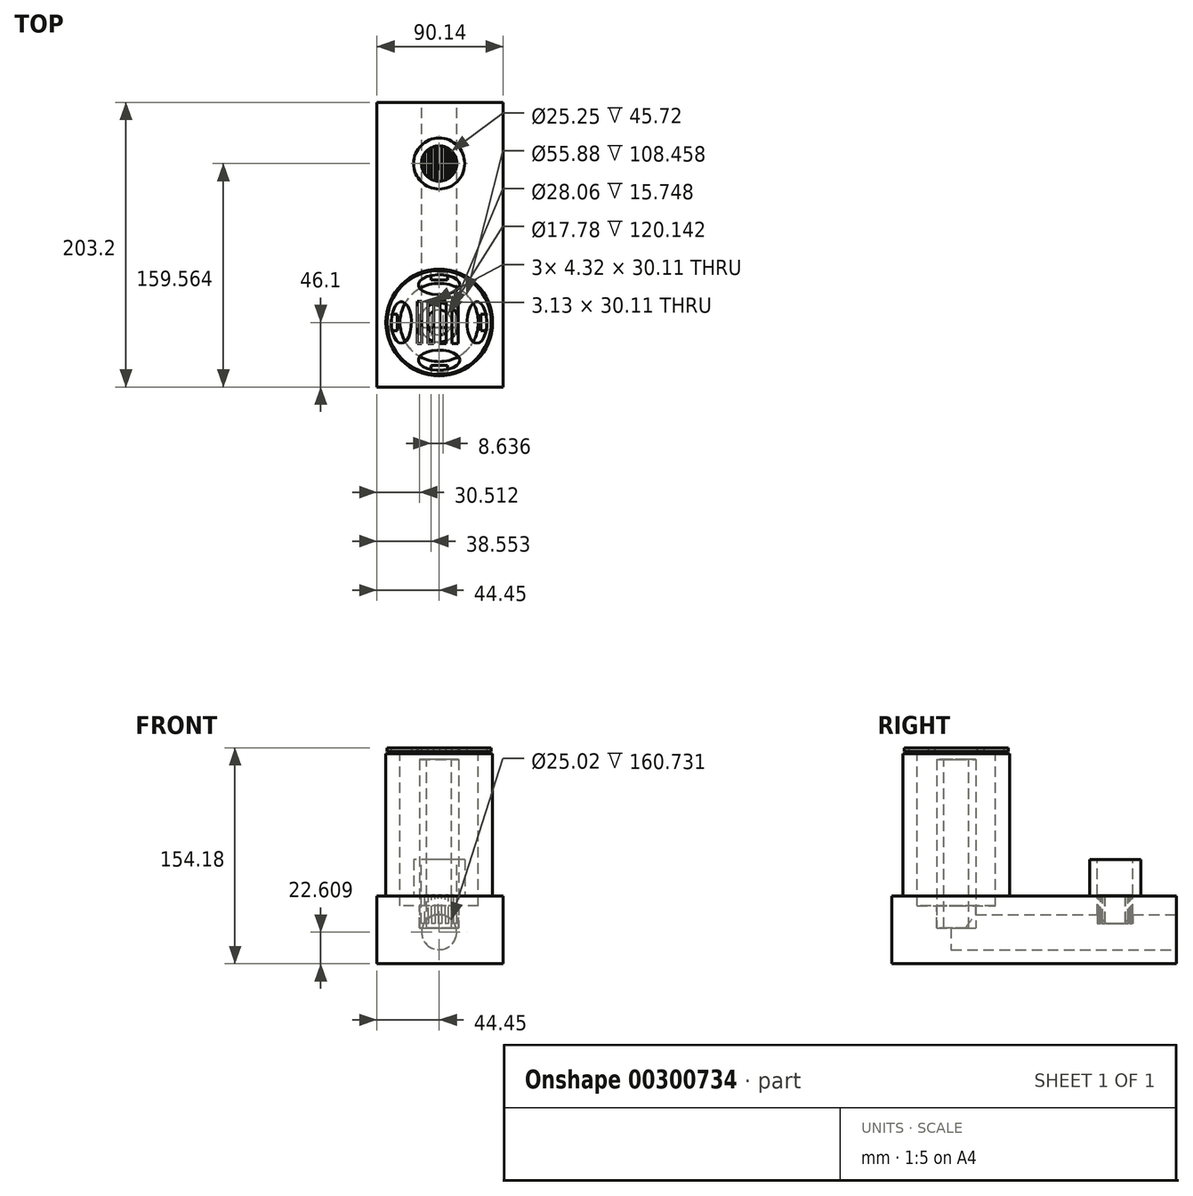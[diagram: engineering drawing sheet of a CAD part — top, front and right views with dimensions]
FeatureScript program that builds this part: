
annotation { "Feature Type Name" : "Feature", "Feature Type Description" : "" }
export const myFeature = defineFeature(function(context is Context, id is Id, definition is map)
    precondition{}
    {
        {
            var Q0;
            Q0=qCreatedBy(makeId("Top.planeOp"),FACE);
            var sketch = newSketch(context, id + "F0", { "sketchPlane" : qUnion([Q0])});
            skCircle(sketch, "E0", {"center": v(0, 0) * mm, "radius": 38.1 * mm});
            skSolve(sketch);
        }
        {
            var Q0;
            Q0=makeQuery(id+"F0.imprint","IMPRINT",FACE,{"disambiguationData":[TD([[makeQuery(id+"F0.imprint","IMPRINT",EDGE,{"derivedFrom":sQuery(id+"F0.wireOp",EDGE,"E0")}),1.0]])]});
            extrude(context, id + "F1", {"entities" : qUnion([Q0]), "depth" : 101.6 * mm});
        }
        {
            var Q0;
            Q0=qCreatedBy(makeId("Top.planeOp"),FACE);
            var sketch = newSketch(context, id + "F2", { "sketchPlane" : qUnion([Q0])});
            skLineSegment(sketch, "E1.bottom", {"start": v(-44.45, -46.1) * mm, "end": v(45.7, -46.1) * mm});
            skLineSegment(sketch, "E1.top", {"start": v(-44.45, 157.1) * mm, "end": v(45.7, 157.1) * mm});
            skLineSegment(sketch, "E1.left", {"start": v(-44.45, -46.1) * mm, "end": v(-44.45, 157.1) * mm});
            skLineSegment(sketch, "E1.right", {"start": v(45.7, -46.1) * mm, "end": v(45.7, 157.1) * mm});
            skSolve(sketch);
        }
        {
            var Q0;
            Q0=makeQuery(id+"F2.imprint","IMPRINT",FACE,{"disambiguationData":[TD([[makeQuery(id+"F2.imprint","IMPRINT",EDGE,{"derivedFrom":sQuery(id+"F2.wireOp",EDGE,"E1.bottom")}),1.0]])]});
            extrude(context, id + "F3", {"entities" : qUnion([Q0]), "operationType" : NewBodyOperationType.ADD, "oppositeDirection" : true, "depth" : 48.26 * mm});
        }
        {
            var Q0;
            Q0=makeQuery(id+"F3.opExtrude","SWEPT_FACE",FACE,{"disambiguationData":[OSD([sQuery(id+"F2.wireOp",EDGE,"E1.top")])]});
            var sketch = newSketch(context, id + "F4", { "sketchPlane" : qUnion([Q0])});
            skCircle(sketch, "E2", {"center": v(0, -25.65) * mm, "radius": 12.5 * mm});
            skSolve(sketch);
        }
        {
            var Q0;
            Q0=makeQuery(id+"F4.imprint","IMPRINT",FACE,{"disambiguationData":[TD([[makeQuery(id+"F4.imprint","IMPRINT",EDGE,{"derivedFrom":sQuery(id+"F4.wireOp",EDGE,"E2")}),1.0]])]});
            extrude(context, id + "F5", {"entities" : qUnion([Q0]), "operationType" : NewBodyOperationType.REMOVE, "oppositeDirection" : true, "depth" : 160.73 * mm});
        }
        {
            var Q0;
            Q0=makeQuery(id+"F1.opExtrude","CAP_FACE",FACE,{"disambiguationData":[OSD([sQuery(id+"F0.wireOp",EDGE,"E0")])],"isStart":false});
            var sketch = newSketch(context, id + "F6", { "sketchPlane" : qUnion([Q0])});
            skCircle(sketch, "E3", {"center": v(0, 0) * mm, "radius": 27.94 * mm});
            skSolve(sketch);
        }
        {
            var Q0;
            Q0=makeQuery(id+"F6.imprint","IMPRINT",FACE,{"disambiguationData":[TD([[makeQuery(id+"F6.imprint","IMPRINT",EDGE,{"derivedFrom":sQuery(id+"F6.wireOp",EDGE,"E3")}),1.0]])]});
            extrude(context, id + "F7", {"entities" : qUnion([Q0]), "operationType" : NewBodyOperationType.REMOVE, "oppositeDirection" : true, "depth" : 108.46 * mm});
        }
        {
            var Q0;
            Q0=makeQuery(id+"F3.opExtrude","CAP_FACE",FACE,{"disambiguationData":[OSD([sQuery(id+"F2.wireOp",EDGE,"E1.bottom"),sQuery(id+"F2.wireOp",EDGE,"E1.top"),sQuery(id+"F2.wireOp",EDGE,"E1.left"),sQuery(id+"F2.wireOp",EDGE,"E1.right")])],"isStart":true});
            var sketch = newSketch(context, id + "F8", { "sketchPlane" : qUnion([Q0])});
            skCircle(sketch, "E4", {"center": v(0, 113.46) * mm, "radius": 18.24 * mm});
            skSolve(sketch);
        }
        {
            var Q0;
            Q0=makeQuery(id+"F8.imprint","IMPRINT",FACE,{"disambiguationData":[TD([[makeQuery(id+"F8.imprint","IMPRINT",EDGE,{"derivedFrom":sQuery(id+"F8.wireOp",EDGE,"E4")}),1.0]])]});
            extrude(context, id + "F9", {"entities" : qUnion([Q0]), "operationType" : NewBodyOperationType.ADD, "depth" : 26.16 * mm});
        }
        {
            var Q0;
            Q0=makeQuery(id+"F9.opExtrude","CAP_FACE",FACE,{"disambiguationData":[OSD([sQuery(id+"F8.wireOp",EDGE,"E4")])],"isStart":false});
            var sketch = newSketch(context, id + "F10", { "sketchPlane" : qUnion([Q0])});
            skCircle(sketch, "E5", {"center": v(0, 113.46) * mm, "radius": 12.62 * mm});
            skSolve(sketch);
        }
        {
            var Q0;
            Q0=makeQuery(id+"F10.imprint","IMPRINT",FACE,{"disambiguationData":[TD([[makeQuery(id+"F10.imprint","IMPRINT",EDGE,{"derivedFrom":sQuery(id+"F10.wireOp",EDGE,"E5")}),1.0]])]});
            extrude(context, id + "F11", {"entities" : qUnion([Q0]), "operationType" : NewBodyOperationType.REMOVE, "oppositeDirection" : true, "depth" : 45.72 * mm});
        }
        {
            var Q0;
            Q0=makeQuery(id+"F7.boolean.opBoolean","COPY",FACE,{"derivedFrom":makeQuery(id+"F7.opExtrude","CAP_FACE",FACE,{"disambiguationData":[OSD([sQuery(id+"F6.wireOp",EDGE,"E3")])],"isStart":false})});
            var sketch = newSketch(context, id + "F12", { "sketchPlane" : qUnion([Q0])});
            skCircle(sketch, "E6", {"center": v(0, 0) * mm, "radius": 14.03 * mm});
            skSolve(sketch);
        }
        {
            var Q0;
            Q0=makeQuery(id+"F12.imprint","IMPRINT",FACE,{"disambiguationData":[TD([[makeQuery(id+"F12.imprint","IMPRINT",EDGE,{"derivedFrom":sQuery(id+"F12.wireOp",EDGE,"E6")}),1.0]])]});
            extrude(context, id + "F13", {"entities" : qUnion([Q0]), "operationType" : NewBodyOperationType.REMOVE, "oppositeDirection" : true, "depth" : 15.75 * mm});
        }
        {
            var Q0;
            Q0=makeQuery(id+"F13.boolean.opBoolean","COPY",FACE,{"derivedFrom":makeQuery(id+"F13.opExtrude","CAP_FACE",FACE,{"disambiguationData":[OSD([sQuery(id+"F12.wireOp",EDGE,"E6")])],"isStart":false})});
            var sketch = newSketch(context, id + "F14", { "sketchPlane" : qUnion([Q0])});
            skCircle(sketch, "E7", {"center": v(0, 0) * mm, "radius": 13.97 * mm});
            skSolve(sketch);
        }
        {
            var Q0;
            Q0 = qSketchRegion(id + "F14", true);
            extrude(context, id + "F15", {"entities" : qUnion([Q0]), "operationType" : NewBodyOperationType.ADD, "depth" : 120.14 * mm});
        }
        {
            var Q0;
            Q0=makeQuery(id+"F15.opExtrude","CAP_FACE",FACE,{"disambiguationData":[OSD([sQuery(id+"F14.wireOp",EDGE,"E7")])],"isStart":false});
            var sketch = newSketch(context, id + "F16", { "sketchPlane" : qUnion([Q0])});
            skCircle(sketch, "E8", {"center": v(0, 0) * mm, "radius": 8.89 * mm});
            skSolve(sketch);
        }
        {
            var Q0;
            Q0=makeQuery(id+"F16.imprint","IMPRINT",FACE,{"disambiguationData":[TD([[makeQuery(id+"F16.imprint","IMPRINT",EDGE,{"derivedFrom":sQuery(id+"F16.wireOp",EDGE,"E8")}),1.0]])]});
            extrude(context, id + "F17", {"entities" : qUnion([Q0]), "operationType" : NewBodyOperationType.REMOVE, "oppositeDirection" : true, "depth" : 120.14 * mm});
        }
        {
            var Q0;
            Q0=makeQuery(id+"F1.opExtrude","CAP_FACE",FACE,{"disambiguationData":[OSD([sQuery(id+"F0.wireOp",EDGE,"E0")])],"isStart":false});
            var sketch = newSketch(context, id + "F18", { "sketchPlane" : qUnion([Q0])});
            skLineSegment(sketch, "E9.bottom", {"start": v(5.84, 30.5) * mm, "end": v(-5.84, 30.5) * mm});
            skLineSegment(sketch, "E9.top", {"start": v(5.84, 35.56) * mm, "end": v(-5.84, 35.56) * mm});
            skLineSegment(sketch, "E9.left", {"start": v(5.84, 30.5) * mm, "end": v(5.84, 35.56) * mm});
            skLineSegment(sketch, "E9.right", {"start": v(-5.84, 30.5) * mm, "end": v(-5.84, 35.56) * mm});
            skPoint(sketch, "E9.middle", {"position": v(0, 33.02) * mm});
            skLineSegment(sketch, "E10.MirrorCS", {"start": v(5.84, -30.5) * mm, "end": v(-5.84, -30.5) * mm});
            skLineSegment(sketch, "E11.MirrorCS", {"start": v(5.84, -35.56) * mm, "end": v(-5.84, -35.56) * mm});
            skLineSegment(sketch, "E12.MirrorCS", {"start": v(-5.84, -30.5) * mm, "end": v(-5.84, -35.56) * mm});
            skLineSegment(sketch, "E13.MirrorCS", {"start": v(5.84, -30.5) * mm, "end": v(5.84, -35.56) * mm});
            skPoint(sketch, "E14.MirrorP", {"position": v(0, -33.02) * mm});
            skLineSegment(sketch, "E15.bottom", {"start": v(34.96, -5.84) * mm, "end": v(29.9, -5.84) * mm});
            skLineSegment(sketch, "E15.top", {"start": v(34.96, 5.84) * mm, "end": v(29.9, 5.84) * mm});
            skLineSegment(sketch, "E15.left", {"start": v(34.96, -5.84) * mm, "end": v(34.96, 5.84) * mm});
            skLineSegment(sketch, "E15.right", {"start": v(29.9, -5.84) * mm, "end": v(29.9, 5.84) * mm});
            skPoint(sketch, "E15.middle", {"position": v(32.43, 0) * mm});
            skLineSegment(sketch, "E16.MirrorCS", {"start": v(-29.9, -5.84) * mm, "end": v(-29.9, 5.84) * mm});
            skLineSegment(sketch, "E17.MirrorCS", {"start": v(-34.96, -5.84) * mm, "end": v(-34.96, 5.84) * mm});
            skLineSegment(sketch, "E18.MirrorCS", {"start": v(-34.96, 5.84) * mm, "end": v(-29.9, 5.84) * mm});
            skLineSegment(sketch, "E19.MirrorCS", {"start": v(-34.96, -5.84) * mm, "end": v(-29.9, -5.84) * mm});
            skPoint(sketch, "E20.MirrorP", {"position": v(-32.43, 0) * mm});
            skSolve(sketch);
        }
        {
            var Q0;
            Q0=makeQuery(id+"F18.imprint","IMPRINT",FACE,{"disambiguationData":[TD([[makeQuery(id+"F18.imprint","IMPRINT",EDGE,{"derivedFrom":sQuery(id+"F18.wireOp",EDGE,"E16.MirrorCS")}),1.0]])]});
            var Q1;
            Q1=makeQuery(id+"F18.imprint","IMPRINT",FACE,{"disambiguationData":[TD([[makeQuery(id+"F18.imprint","IMPRINT",EDGE,{"derivedFrom":sQuery(id+"F18.wireOp",EDGE,"E9.bottom")}),-1.0]])]});
            var Q2;
            Q2=makeQuery(id+"F18.imprint","IMPRINT",FACE,{"disambiguationData":[TD([[makeQuery(id+"F18.imprint","IMPRINT",EDGE,{"derivedFrom":sQuery(id+"F18.wireOp",EDGE,"E15.bottom")}),-1.0]])]});
            var Q3;
            Q3=makeQuery(id+"F18.imprint","IMPRINT",FACE,{"disambiguationData":[TD([[makeQuery(id+"F18.imprint","IMPRINT",EDGE,{"derivedFrom":sQuery(id+"F18.wireOp",EDGE,"E10.MirrorCS")}),1.0]])]});
            extrude(context, id + "F19", {"entities" : qUnion([Q0, Q1, Q2, Q3]), "operationType" : NewBodyOperationType.ADD, "depth" : 1.78 * mm});
        }
        {
            var Q0;
            Q0=makeQuery(id+"F19.opExtrude","CAP_FACE",FACE,{"disambiguationData":[OSD([sQuery(id+"F18.wireOp",EDGE,"E10.MirrorCS"),sQuery(id+"F18.wireOp",EDGE,"E11.MirrorCS"),sQuery(id+"F18.wireOp",EDGE,"E12.MirrorCS"),sQuery(id+"F18.wireOp",EDGE,"E13.MirrorCS")])],"isStart":false});
            var sketch = newSketch(context, id + "F20", { "sketchPlane" : qUnion([Q0])});
            skCircle(sketch, "E21", {"center": v(0, 0) * mm, "radius": 37.13 * mm});
            skSolve(sketch);
        }
        {
            var Q0;
            Q0 = qSketchRegion(id + "F20", true);
            extrude(context, id + "F21", {"entities" : qUnion([Q0]), "operationType" : NewBodyOperationType.ADD, "depth" : 2.54 * mm});
        }
        {
            var Q0;
            Q0=makeQuery(id+"F21.opExtrude","CAP_FACE",FACE,{"disambiguationData":[OSD([sQuery(id+"F20.wireOp",EDGE,"E21")])],"isStart":false});
            var sketch = newSketch(context, id + "F22", { "sketchPlane" : qUnion([Q0])});
            skEllipse(sketch, "E22", {"center": v(-26.95, 0) * mm, "majorRadius": 14.9 * mm, "minorRadius": 7.14 * mm, "majorAxis": v(0, -1)});
            skEllipse(sketch, "E23.MirrorC", {"center": v(26.95, 0) * mm, "majorRadius": 14.9 * mm, "minorRadius": 7.14 * mm, "majorAxis": v(0, -1)});
            skEllipse(sketch, "E24", {"center": v(0, 26.94) * mm, "majorRadius": 14.9 * mm, "minorRadius": 7.14 * mm, "majorAxis": v(1, 0)});
            skEllipse(sketch, "E25.MirrorC", {"center": v(0, -26.94) * mm, "majorRadius": 14.9 * mm, "minorRadius": 7.14 * mm, "majorAxis": v(1, 0)});
            skLineSegment(sketch, "E26.bottom", {"start": v(15.5, -15.05) * mm, "end": v(-15.5, -15.05) * mm});
            skLineSegment(sketch, "E26.top", {"start": v(15.5, 15.05) * mm, "end": v(-15.5, 15.05) * mm});
            skLineSegment(sketch, "E26.left", {"start": v(15.5, -15.05) * mm, "end": v(15.5, 15.05) * mm});
            skLineSegment(sketch, "E26.right", {"start": v(-15.5, -15.05) * mm, "end": v(-15.5, 15.05) * mm});
            skPoint(sketch, "E26.middle", {"position": v(0, 0) * mm});
            skLineSegment(sketch, "E27", {"start": v(-12.37, 15.05) * mm, "end": v(-12.37, -15.05) * mm});
            skLineSegment(sketch, "E28", {"start": v(-8.06, 15.05) * mm, "end": v(-8.06, -15.05) * mm});
            skLineSegment(sketch, "E29", {"start": v(-3.74, 15.05) * mm, "end": v(-3.74, -15.05) * mm});
            skLineSegment(sketch, "E30", {"start": v(0.58, 15.05) * mm, "end": v(0.58, -15.05) * mm});
            skLineSegment(sketch, "E31", {"start": v(9.22, 15.05) * mm, "end": v(9.22, -15.05) * mm});
            skLineSegment(sketch, "E32", {"start": v(4.9, 15.05) * mm, "end": v(4.9, -15.05) * mm});
            skLineSegment(sketch, "E33", {"start": v(13.53, 15.05) * mm, "end": v(13.53, -15.05) * mm});
            skSolve(sketch);
        }
        {
            var Q0;
            Q0=makeQuery(id+"F22.imprint","IMPRINT",FACE,{"disambiguationData":[TD([[makeQuery(id+"F22.imprint","IMPRINT",EDGE,{"derivedFrom":sQuery(id+"F22.wireOp",EDGE,"E24")}),1.0]])]});
            var Q1;
            Q1=makeQuery(id+"F22.imprint","IMPRINT",FACE,{"disambiguationData":[TD([[makeQuery(id+"F22.imprint","IMPRINT",EDGE,{"derivedFrom":sQuery(id+"F22.wireOp",EDGE,"E22")}),1.0]])]});
            var Q2;
            {var subQ0=sQuery(id+"F22.wireOp",EDGE,"E26.right");Q2=makeQuery(id+"F22.imprint","IMPRINT",FACE,{"disambiguationData":[TD([[makeQuery(id+"F22.imprint","IMPRINT",EDGE,{"derivedFrom":subQ0}),-1.0]])]});}
            var Q3;
            {var subQ0=sQuery(id+"F22.wireOp",EDGE,"E28");Q3=makeQuery(id+"F22.imprint","IMPRINT",FACE,{"disambiguationData":[TD([[makeQuery(id+"F22.imprint","IMPRINT",EDGE,{"derivedFrom":subQ0}),1.0]])]});}
            var Q4;
            {var subQ0=sQuery(id+"F22.wireOp",EDGE,"E30");Q4=makeQuery(id+"F22.imprint","IMPRINT",FACE,{"disambiguationData":[TD([[makeQuery(id+"F22.imprint","IMPRINT",EDGE,{"derivedFrom":subQ0}),1.0]])]});}
            var Q5;
            {var subQ0=sQuery(id+"F22.wireOp",EDGE,"E31");Q5=makeQuery(id+"F22.imprint","IMPRINT",FACE,{"disambiguationData":[TD([[makeQuery(id+"F22.imprint","IMPRINT",EDGE,{"derivedFrom":subQ0}),1.0]])]});}
            var Q6;
            Q6=makeQuery(id+"F22.imprint","IMPRINT",FACE,{"disambiguationData":[TD([[makeQuery(id+"F22.imprint","IMPRINT",EDGE,{"derivedFrom":sQuery(id+"F22.wireOp",EDGE,"E23.MirrorC")}),1.0]])]});
            var Q7;
            Q7=makeQuery(id+"F22.imprint","IMPRINT",FACE,{"disambiguationData":[TD([[makeQuery(id+"F22.imprint","IMPRINT",EDGE,{"derivedFrom":sQuery(id+"F22.wireOp",EDGE,"E25.MirrorC")}),1.0]])]});
            extrude(context, id + "F23", {"entities" : qUnion([Q0, Q1, Q2, Q3, Q4, Q5, Q6, Q7]), "operationType" : NewBodyOperationType.REMOVE, "oppositeDirection" : true, "depth" : 3.56 * mm});
        }
        {
            var Q0;
            Q0=makeQuery(id+"F11.boolean.opBoolean","COPY",FACE,{"disambiguationData":[OD(0.0)],"derivedFrom":makeQuery(id+"F11.opExtrude","CAP_FACE",FACE,{"disambiguationData":[OSD([sQuery(id+"F10.wireOp",EDGE,"E5")])],"isStart":false})});
            var sketch = newSketch(context, id + "F24", { "sketchPlane" : qUnion([Q0])});
            skLineSegment(sketch, "E34.bottom", {"start": v(12.7, 100.76) * mm, "end": v(-12.7, 100.76) * mm});
            skLineSegment(sketch, "E34.top", {"start": v(12.7, 126.16) * mm, "end": v(-12.7, 126.16) * mm});
            skLineSegment(sketch, "E34.left", {"start": v(12.7, 100.76) * mm, "end": v(12.7, 126.16) * mm});
            skLineSegment(sketch, "E34.right", {"start": v(-12.7, 100.76) * mm, "end": v(-12.7, 126.16) * mm});
            skPoint(sketch, "E34.middle", {"position": v(0, 113.46) * mm});
            skLineSegment(sketch, "E35", {"start": v(-10.16, 121.08) * mm, "end": v(-10.16, 105.84) * mm});
            skLineSegment(sketch, "E36", {"start": v(-7.62, 123.62) * mm, "end": v(-7.62, 103.3) * mm});
            skCircle(sketch, "E37", {"center": v(0, 113.46) * mm, "radius": 12.7 * mm});
            skLineSegment(sketch, "E38", {"start": v(-5.45, 124.94) * mm, "end": v(-5.45, 102) * mm});
            skLineSegment(sketch, "E39", {"start": v(-3.05, 125.8) * mm, "end": v(-3.05, 101.14) * mm});
            skLineSegment(sketch, "E40", {"start": v(-0.54, 126.15) * mm, "end": v(-0.54, 100.78) * mm});
            skLineSegment(sketch, "E41", {"start": v(2, 126) * mm, "end": v(2, 100.92) * mm});
            skLineSegment(sketch, "E42", {"start": v(4.45, 125.36) * mm, "end": v(4.45, 101.57) * mm});
            skLineSegment(sketch, "E43", {"start": v(6.73, 124.23) * mm, "end": v(6.73, 102.7) * mm});
            skLineSegment(sketch, "E44", {"start": v(8.74, 122.68) * mm, "end": v(8.74, 104.25) * mm});
            skLineSegment(sketch, "E45", {"start": v(10.4, 120.76) * mm, "end": v(10.4, 106.17) * mm});
            skSolve(sketch);
        }
        {
            var Q0;
            {var subQ0=sQuery(id+"F24.wireOp",EDGE,"E35");Q0=makeQuery(id+"F24.imprint","IMPRINT",FACE,{"disambiguationData":[TD([[makeQuery(id+"F24.imprint","IMPRINT",EDGE,{"derivedFrom":subQ0}),1.0]])]});}
            var Q1;
            {var subQ0=sQuery(id+"F24.wireOp",EDGE,"E38");Q1=makeQuery(id+"F24.imprint","IMPRINT",FACE,{"disambiguationData":[TD([[makeQuery(id+"F24.imprint","IMPRINT",EDGE,{"derivedFrom":subQ0}),1.0]])]});}
            var Q2;
            {var subQ3=sQuery(id+"F24.wireOp",EDGE,"E40");Q2=makeQuery(id+"F24.imprint","IMPRINT",FACE,{"disambiguationData":[TD([[makeQuery(id+"F24.imprint","IMPRINT",EDGE,{"derivedFrom":subQ3}),1.0]])]});}
            var Q3;
            {var subQ0=sQuery(id+"F24.wireOp",EDGE,"E42");Q3=makeQuery(id+"F24.imprint","IMPRINT",FACE,{"disambiguationData":[TD([[makeQuery(id+"F24.imprint","IMPRINT",EDGE,{"derivedFrom":subQ0}),1.0]])]});}
            var Q4;
            {var subQ0=sQuery(id+"F24.wireOp",EDGE,"E44");Q4=makeQuery(id+"F24.imprint","IMPRINT",FACE,{"disambiguationData":[TD([[makeQuery(id+"F24.imprint","IMPRINT",EDGE,{"derivedFrom":subQ0}),1.0]])]});}
            extrude(context, id + "F25", {"entities" : qUnion([Q0, Q1, Q2, Q3, Q4]), "operationType" : NewBodyOperationType.ADD, "depth" : 20.32 * mm});
        }
    });
